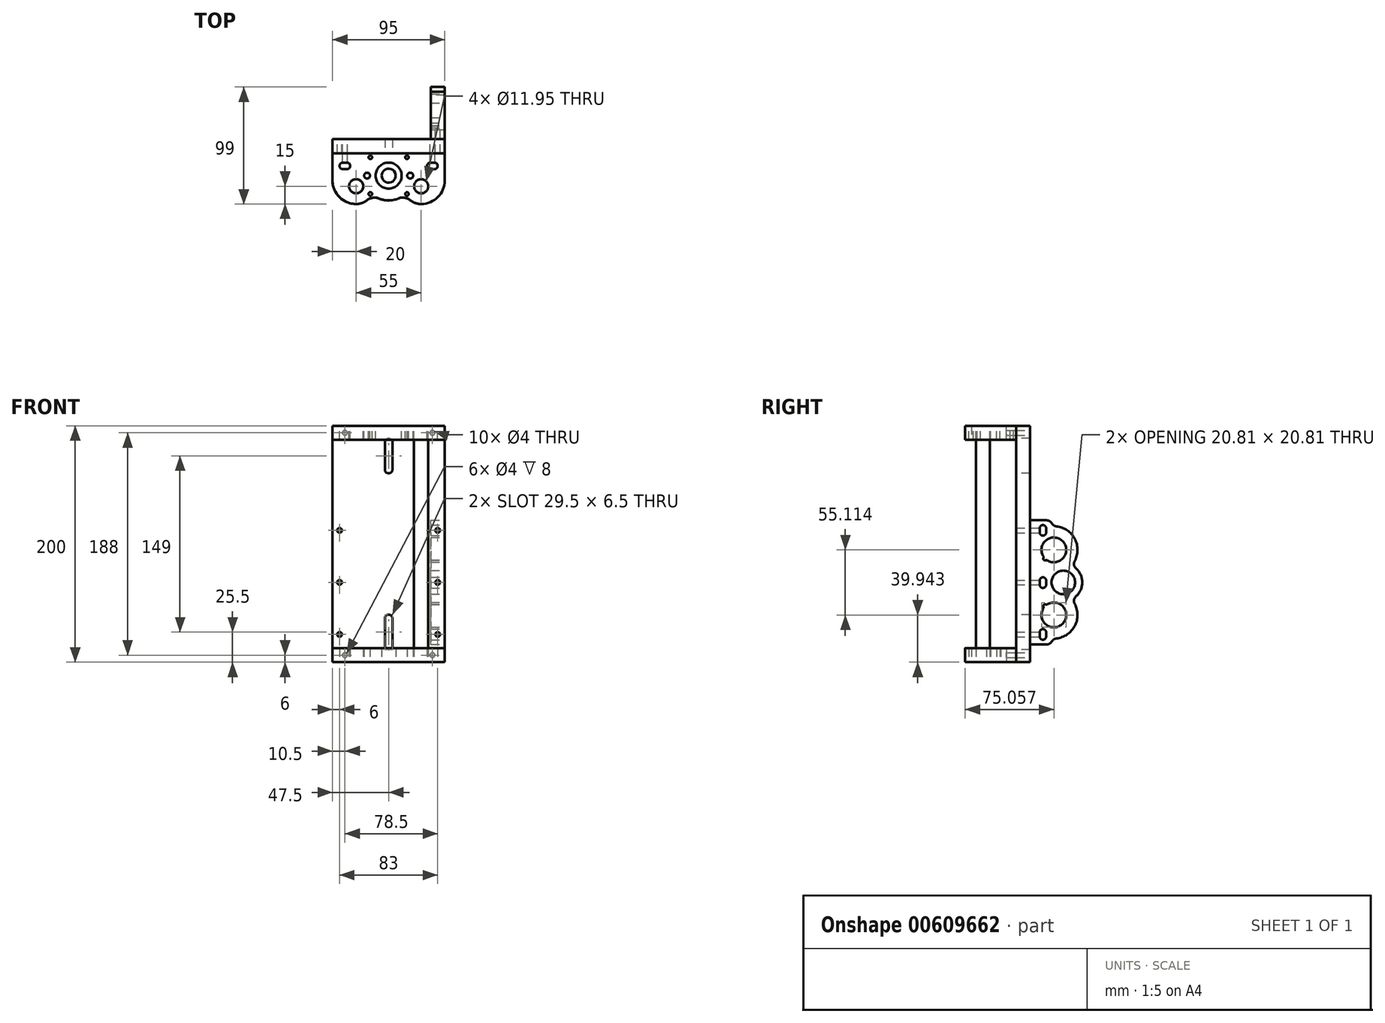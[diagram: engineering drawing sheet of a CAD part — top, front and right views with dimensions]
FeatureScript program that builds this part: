
annotation { "Feature Type Name" : "Feature", "Feature Type Description" : "" }
export const myFeature = defineFeature(function(context is Context, id is Id, definition is map)
    precondition{}
    {
        {
            var Q0;
            Q0=qCreatedBy(makeId("Front.planeOp"),FACE);
            var sketch = newSketch(context, id + "F0", { "sketchPlane" : qUnion([Q0])});
            skLineSegment(sketch, "E0.bottom", {"start": v(47.5, 0) * mm, "end": v(-47.5, 0) * mm});
            skLineSegment(sketch, "E0.top", {"start": v(-47.5, 200) * mm, "end": v(47.5, 200) * mm});
            skLineSegment(sketch, "E0.left", {"start": v(-47.5, 0) * mm, "end": v(-47.5, 200) * mm});
            skLineSegment(sketch, "E0.right", {"start": v(47.5, 0) * mm, "end": v(47.5, 200) * mm});
            skLineSegment(sketch, "E1.left", {"start": v(3.25, 186) * mm, "end": v(3.25, 163) * mm});
            skLineSegment(sketch, "E1.right", {"start": v(-3.25, 186) * mm, "end": v(-3.25, 163) * mm});
            skArc(sketch, "E2", {"start": v(3.25, 186) * mm, "mid": v(0, 189.25) * mm, "end": v(-3.25, 186) * mm});
            skArc(sketch, "E3", {"start": v(-3.25, 163) * mm, "mid": v(0, 159.75) * mm, "end": v(3.25, 163) * mm});
            skLineSegment(sketch, "E4", {"start": v(0, 200) * mm, "end": v(0, 186) * mm, "construction": true});
            skLineSegment(sketch, "E5.left", {"start": v(-3.25, 14) * mm, "end": v(-3.25, 37) * mm});
            skLineSegment(sketch, "E5.right", {"start": v(3.25, 14) * mm, "end": v(3.25, 37) * mm});
            skArc(sketch, "E6", {"start": v(-3.25, 14) * mm, "mid": v(0, 10.75) * mm, "end": v(3.25, 14) * mm});
            skArc(sketch, "E7", {"start": v(3.25, 37) * mm, "mid": v(0, 40.25) * mm, "end": v(-3.25, 37) * mm});
            skLineSegment(sketch, "E8", {"start": v(0, 0) * mm, "end": v(0, 14) * mm, "construction": true});
            skSolve(sketch);
        }
        {
            var Q0;
            Q0=qSketchRegion(id+"F0",true);
            extrude(context, id + "F1", {"entities" : qUnion([Q0]), "oppositeDirection" : true, "depth" : 12 * mm, "offsetDistance" : 25 * mm});
        }
        {
            var Q0;
            Q0=makeQuery(id+"F1.opExtrude","SWEPT_FACE",FACE,{"disambiguationData":[OSD([sQuery(id+"F0.wireOp",EDGE,"E0.top")])]});
            var sketch = newSketch(context, id + "F2", { "sketchPlane" : qUnion([Q0])});
            skLineSegment(sketch, "E9.bottom", {"start": v(-47.5, 0) * mm, "end": v(47.5, 0) * mm});
            skLineSegment(sketch, "E9.top", {"start": v(-27.5, -43) * mm, "end": v(27.5, -43) * mm, "construction": true});
            skLineSegment(sketch, "E9.left", {"start": v(-47.5, 0) * mm, "end": v(-47.5, -23) * mm});
            skLineSegment(sketch, "E9.right", {"start": v(47.5, 0) * mm, "end": v(47.5, -23) * mm});
            skLineSegment(sketch, "E10", {"start": v(0, 0) * mm, "end": v(0, -43) * mm, "construction": true});
            skCircle(sketch, "E11", {"center": v(-27.5, -28) * mm, "radius": 5.97 * mm});
            skCircle(sketch, "E12.MirrorC", {"center": v(27.5, -28) * mm, "radius": 5.97 * mm});
            skArc(sketch, "E13.filletArc", {"start": v(-47.5, -23) * mm, "mid": v(-41.64, -37.14) * mm, "end": v(-27.5, -43) * mm});
            skPoint(sketch, "E14.visualSharp", {"position": v(47.5, -43) * mm});
            skArc(sketch, "E14.filletArc", {"start": v(27.5, -43) * mm, "mid": v(41.64, -37.14) * mm, "end": v(47.5, -23) * mm});
            skCircle(sketch, "E15", {"center": v(0, -19) * mm, "radius": 11 * mm});
            skCircle(sketch, "E16", {"center": v(-18.25, -19) * mm, "radius": 2.5 * mm});
            skCircle(sketch, "E17.MirrorC", {"center": v(18.25, -19) * mm, "radius": 2.5 * mm});
            skLineSegment(sketch, "E18.bottom", {"start": v(-38.75, -8) * mm, "end": v(-35.25, -8) * mm});
            skLineSegment(sketch, "E18.top", {"start": v(-38.75, -13.5) * mm, "end": v(-35.25, -13.5) * mm});
            skArc(sketch, "E19", {"start": v(-38.75, -8) * mm, "mid": v(-41.5, -10.75) * mm, "end": v(-38.75, -13.5) * mm});
            skArc(sketch, "E20", {"start": v(-35.25, -13.5) * mm, "mid": v(-32.5, -10.75) * mm, "end": v(-35.25, -8) * mm});
            skLineSegment(sketch, "E21", {"start": v(-37, -8) * mm, "end": v(-37, -13.5) * mm, "construction": true});
            skArc(sketch, "E22.MirrorCS", {"start": v(35.25, -13.5) * mm, "mid": v(32.5, -10.75) * mm, "end": v(35.25, -8) * mm});
            skLineSegment(sketch, "E23.MirrorCS", {"start": v(38.75, -13.5) * mm, "end": v(35.25, -13.5) * mm});
            skLineSegment(sketch, "E24.MirrorCS", {"start": v(38.75, -8) * mm, "end": v(35.25, -8) * mm});
            skArc(sketch, "E25.MirrorCS", {"start": v(38.75, -8) * mm, "mid": v(41.5, -10.75) * mm, "end": v(38.75, -13.5) * mm});
            skArc(sketch, "E26", {"start": v(-8.94, 0) * mm, "mid": v(0, -40) * mm, "end": v(8.94, 0) * mm});
            skCircle(sketch, "E27", {"center": v(-27.5, -28) * mm, "radius": 15 * mm});
            skCircle(sketch, "E28", {"center": v(27.5, -28) * mm, "radius": 15 * mm});
            skSolve(sketch);
        }
        {
            var Q0;
            Q0=qSketchRegion(id+"F2",true);
            extrude(context, id + "F3", {"entities" : qUnion([Q0]), "oppositeDirection" : true, "depth" : 12 * mm, "offsetDistance" : 25 * mm});
        }
        {
            var Q0;
            Q0=makeQuery(id+"F3.opExtrude","SWEPT_EDGE",EDGE,{"disambiguationData":[OSD([sQuery(id+"F2.wireOp",EDGE,"E26"),sQuery(id+"F2.wireOp",EDGE,"E27")])]});
            var Q1;
            Q1=makeQuery(id+"F3.opExtrude","SWEPT_EDGE",EDGE,{"disambiguationData":[OSD([sQuery(id+"F2.wireOp",EDGE,"E26"),sQuery(id+"F2.wireOp",EDGE,"E28")])]});
            fillet(context, id + "F4", {"entities" : qUnion([Q0, Q1]), "radius" : 10 * mm, "tangentPropagation" : true, "allowEdgeOverflow" : false});
        }
        {
            var Q0;
            Q0=makeQuery(id+"F3.opExtrude","CAP_FACE",FACE,{"disambiguationData":[OSD([sQuery(id+"F2.wireOp",EDGE,"E9.bottom"),sQuery(id+"F2.wireOp",EDGE,"E9.top"),sQuery(id+"F2.wireOp",EDGE,"E9.left"),sQuery(id+"F2.wireOp",EDGE,"E9.right"),sQuery(id+"F2.wireOp",EDGE,"E11"),sQuery(id+"F2.wireOp",EDGE,"E12.MirrorC"),sQuery(id+"F2.wireOp",EDGE,"E13.filletArc"),sQuery(id+"F2.wireOp",EDGE,"E14.filletArc")])],"isStart":true});
            var sketch = newSketch(context, id + "F5", { "sketchPlane" : qUnion([Q0])});
            skCircle(sketch, "E29", {"center": v(27.5, -28) * mm, "radius": 6 * mm});
            skSolve(sketch);
        }
        {
            var Q0;
            Q0=qSketchRegion(id+"F5",true);
            extrude(context, id + "F6", {"entities" : qUnion([Q0]), "oppositeDirection" : true, "depth" : 188 * mm, "offsetDistance" : 25 * mm});
        }
        {
            var Q0;
            Q0=makeQuery(id+"F1.opExtrude","SWEPT_FACE",FACE,{"disambiguationData":[OSD([sQuery(id+"F0.wireOp",EDGE,"E0.right")])]});
            var sketch = newSketch(context, id + "F7", { "sketchPlane" : qUnion([Q0])});
            skLineSegment(sketch, "E30.top", {"start": v(52, 40) * mm, "end": v(52, 67.5) * mm, "construction": true});
            skLineSegment(sketch, "E31", {"start": v(12, 67.5) * mm, "end": v(52, 67.5) * mm, "construction": true});
            skPoint(sketch, "E32.centerSnap0", {"position": v(32, 67.5) * mm});
            skArc(sketch, "E33.filletArc", {"start": v(32, 20) * mm, "mid": v(46.14, 25.86) * mm, "end": v(52, 40) * mm});
            skArc(sketch, "E34.filletArc", {"start": v(52, 95) * mm, "mid": v(46.14, 109.14) * mm, "end": v(32, 115) * mm});
            skArc(sketch, "E35", {"start": v(23.22, 45.7) * mm, "mid": v(39.4, 32.6) * mm, "end": v(26.3, 48.78) * mm});
            skArc(sketch, "E36.MirrorC", {"start": v(23.22, 89.3) * mm, "mid": v(39.4, 102.4) * mm, "end": v(26.3, 86.22) * mm});
            skArc(sketch, "E37", {"start": v(47.07, 53.15) * mm, "mid": v(56, 67.5) * mm, "end": v(47.07, 81.85) * mm});
            skCircle(sketch, "E38", {"center": v(40, 67.5) * mm, "radius": 9.97 * mm});
            skLineSegment(sketch, "E39.bottom", {"start": v(32, 20) * mm, "end": v(28.5, 15) * mm});
            skLineSegment(sketch, "E39.right", {"start": v(28.5, 15) * mm, "end": v(12, 15) * mm});
            skLineSegment(sketch, "E40.bottom", {"start": v(25.5, 25.25) * mm, "end": v(25.5, 21.75) * mm});
            skLineSegment(sketch, "E40.top", {"start": v(20, 25.25) * mm, "end": v(20, 21.75) * mm});
            skArc(sketch, "E41", {"start": v(25.5, 25.25) * mm, "mid": v(22.75, 28) * mm, "end": v(20, 25.25) * mm});
            skArc(sketch, "E42", {"start": v(20, 21.75) * mm, "mid": v(22.75, 19) * mm, "end": v(25.5, 21.75) * mm});
            skLineSegment(sketch, "E43.MirrorCS", {"start": v(32, 115) * mm, "end": v(28.5, 120) * mm});
            skLineSegment(sketch, "E44.MirrorCS", {"start": v(28.5, 120) * mm, "end": v(12, 120) * mm});
            skLineSegment(sketch, "E45.top", {"start": v(20, 69.07) * mm, "end": v(20, 65.57) * mm});
            skArc(sketch, "E46", {"start": v(25.5, 69.07) * mm, "mid": v(22.75, 71.82) * mm, "end": v(20, 69.07) * mm});
            skArc(sketch, "E47", {"start": v(20, 65.57) * mm, "mid": v(22.75, 62.82) * mm, "end": v(25.5, 65.57) * mm});
            skLineSegment(sketch, "E48", {"start": v(20, 23.5) * mm, "end": v(25.5, 23.5) * mm, "construction": true});
            skLineSegment(sketch, "E49.trimOffspring", {"start": v(52, 67.5) * mm, "end": v(52, 95) * mm, "construction": true});
            skLineSegment(sketch, "E50", {"start": v(12, 120) * mm, "end": v(12, 15) * mm});
            skLineSegment(sketch, "E51", {"start": v(32, 40) * mm, "end": v(32, 20) * mm, "construction": true});
            skLineSegment(sketch, "E52", {"start": v(32, 95) * mm, "end": v(32, 40) * mm, "construction": true});
            skArc(sketch, "E53", {"start": v(52, 40) * mm, "mid": v(50.73, 47.02) * mm, "end": v(47.07, 53.15) * mm});
            skArc(sketch, "E54.MirrorCS", {"start": v(52, 95) * mm, "mid": v(50.73, 87.98) * mm, "end": v(47.07, 81.85) * mm});
            skLineSegment(sketch, "E55", {"start": v(32, 95) * mm, "end": v(24.6, 87.6) * mm, "construction": true});
            skArc(sketch, "E56", {"start": v(23.26, 88.29) * mm, "mid": v(23.53, 86.53) * mm, "end": v(25.29, 86.26) * mm});
            skPoint(sketch, "E57.visualSharp", {"position": v(23.61, 88.73) * mm});
            skArc(sketch, "E57.filletArc", {"start": v(23.26, 88.29) * mm, "mid": v(23.38, 88.8) * mm, "end": v(23.22, 89.3) * mm});
            skPoint(sketch, "E58.visualSharp", {"position": v(25.73, 86.61) * mm});
            skArc(sketch, "E58.filletArc", {"start": v(26.3, 86.22) * mm, "mid": v(25.8, 86.38) * mm, "end": v(25.29, 86.26) * mm});
            skArc(sketch, "E59.MirrorCS", {"start": v(26.3, 48.78) * mm, "mid": v(25.8, 48.62) * mm, "end": v(25.29, 48.74) * mm});
            skArc(sketch, "E60.MirrorCS", {"start": v(23.26, 46.71) * mm, "mid": v(23.53, 48.47) * mm, "end": v(25.29, 48.74) * mm});
            skArc(sketch, "E61.MirrorCS", {"start": v(23.26, 46.71) * mm, "mid": v(23.38, 46.2) * mm, "end": v(23.22, 45.7) * mm});
            skLineSegment(sketch, "E62", {"start": v(25.5, 69.07) * mm, "end": v(25.5, 65.57) * mm});
            skArc(sketch, "E63.MirrorCS", {"start": v(25.5, 109.75) * mm, "mid": v(22.75, 107) * mm, "end": v(20, 109.75) * mm});
            skLineSegment(sketch, "E64.MirrorCS", {"start": v(25.5, 109.75) * mm, "end": v(25.5, 113.25) * mm});
            skLineSegment(sketch, "E65.MirrorCS", {"start": v(20, 109.75) * mm, "end": v(20, 113.25) * mm});
            skArc(sketch, "E66.MirrorCS", {"start": v(20, 113.25) * mm, "mid": v(22.75, 116) * mm, "end": v(25.5, 113.25) * mm});
            skSolve(sketch);
        }
        {
            var Q0;
            Q0=qSketchRegion(id+"F7",true);
            extrude(context, id + "F8", {"entities" : qUnion([Q0]), "oppositeDirection" : true, "depth" : 12 * mm, "offsetDistance" : 25 * mm});
        }
        {
            var Q0;
            Q0=makeQuery(id+"F1.opExtrude","SWEPT_FACE",FACE,{"disambiguationData":[OSD([sQuery(id+"F0.wireOp",EDGE,"E0.bottom")])]});
            var sketch = newSketch(context, id + "F9", { "sketchPlane" : qUnion([Q0])});
            skLineSegment(sketch, "E67.0", {"start": v(-47.5, 0) * mm, "end": v(47.5, 0) * mm});
            skArc(sketch, "E67.1", {"start": v(47.5, 23) * mm, "mid": v(41.64, 37.14) * mm, "end": v(27.5, 43) * mm});
            skLineSegment(sketch, "E67.3", {"start": v(47.5, 0) * mm, "end": v(47.5, 23) * mm});
            skArc(sketch, "E67.4", {"start": v(-27.5, 43) * mm, "mid": v(-41.64, 37.14) * mm, "end": v(-47.5, 23) * mm});
            skLineSegment(sketch, "E67.5", {"start": v(-47.5, 23) * mm, "end": v(-47.5, 0) * mm});
            skCircle(sketch, "E68.0", {"center": v(-27.5, 28) * mm, "radius": 5.97 * mm});
            skCircle(sketch, "E69.0", {"center": v(27.5, 28) * mm, "radius": 5.97 * mm});
            skCircle(sketch, "E70.0", {"center": v(-18.25, 19) * mm, "radius": 2.5 * mm});
            skCircle(sketch, "E71.0", {"center": v(18.25, 19) * mm, "radius": 2.5 * mm});
            skCircle(sketch, "E72.0", {"center": v(0, 19) * mm, "radius": 6 * mm});
            skArc(sketch, "E73.0", {"start": v(18.18, 39.76) * mm, "mid": v(22.57, 42.17) * mm, "end": v(27.5, 43) * mm});
            skArc(sketch, "E73.1", {"start": v(-27.5, 43) * mm, "mid": v(-22.57, 42.17) * mm, "end": v(-18.18, 39.76) * mm});
            skArc(sketch, "E73.2", {"start": v(-18.18, 39.76) * mm, "mid": v(-13.34, 37.69) * mm, "end": v(-8.11, 38.37) * mm});
            skArc(sketch, "E73.3", {"start": v(-8.11, 38.37) * mm, "mid": v(0, 40) * mm, "end": v(8.11, 38.37) * mm});
            skArc(sketch, "E73.4", {"start": v(8.11, 38.37) * mm, "mid": v(13.34, 37.69) * mm, "end": v(18.18, 39.76) * mm});
            skArc(sketch, "E74.0", {"start": v(-38.75, 8) * mm, "mid": v(-41.5, 10.75) * mm, "end": v(-38.75, 13.5) * mm});
            skLineSegment(sketch, "E74.1", {"start": v(-38.75, 8) * mm, "end": v(-35.25, 8) * mm});
            skArc(sketch, "E74.2", {"start": v(-35.25, 13.5) * mm, "mid": v(-32.5, 10.75) * mm, "end": v(-35.25, 8) * mm});
            skLineSegment(sketch, "E74.3", {"start": v(-38.75, 13.5) * mm, "end": v(-35.25, 13.5) * mm});
            skArc(sketch, "E75.0", {"start": v(35.25, 13.5) * mm, "mid": v(32.5, 10.75) * mm, "end": v(35.25, 8) * mm});
            skLineSegment(sketch, "E75.1", {"start": v(38.75, 13.5) * mm, "end": v(35.25, 13.5) * mm});
            skArc(sketch, "E75.2", {"start": v(38.75, 8) * mm, "mid": v(41.5, 10.75) * mm, "end": v(38.75, 13.5) * mm});
            skLineSegment(sketch, "E75.3", {"start": v(38.75, 8) * mm, "end": v(35.25, 8) * mm});
            skSolve(sketch);
        }
        {
            var Q0;
            Q0=qSketchRegion(id+"F9",true);
            extrude(context, id + "F10", {"entities" : qUnion([Q0]), "oppositeDirection" : true, "depth" : 12 * mm, "offsetDistance" : 25 * mm});
        }
        {
            var Q0;
            Q0=makeQuery(id+"F1.opExtrude","CAP_FACE",FACE,{"disambiguationData":[OSD([sQuery(id+"F0.wireOp",EDGE,"E0.bottom"),sQuery(id+"F0.wireOp",EDGE,"E0.top"),sQuery(id+"F0.wireOp",EDGE,"E0.left"),sQuery(id+"F0.wireOp",EDGE,"E0.right")])],"isStart":false});
            var sketch = newSketch(context, id + "F11", { "sketchPlane" : qUnion([Q0])});
            skCircle(sketch, "E76", {"center": v(-37, 194) * mm, "radius": 2 * mm});
            skCircle(sketch, "E77", {"center": v(37, 194) * mm, "radius": 2 * mm});
            skLineSegment(sketch, "E78", {"start": v(-47.5, 100) * mm, "end": v(47.5, 100) * mm, "construction": true});
            skCircle(sketch, "E79.MirrorC", {"center": v(37, 6) * mm, "radius": 2 * mm});
            skCircle(sketch, "E80.MirrorC", {"center": v(-37, 6) * mm, "radius": 2 * mm});
            skCircle(sketch, "E81", {"center": v(-41.5, 23.5) * mm, "radius": 2 * mm});
            skCircle(sketch, "E82", {"center": v(-41.5, 111.5) * mm, "radius": 2 * mm});
            skCircle(sketch, "E83", {"center": v(-41.5, 67.5) * mm, "radius": 2 * mm});
            skLineSegment(sketch, "E84", {"start": v(0, 100) * mm, "end": v(0, 0) * mm, "construction": true});
            skCircle(sketch, "E85.MirrorC", {"center": v(41.5, 23.5) * mm, "radius": 2 * mm});
            skCircle(sketch, "E86.MirrorC", {"center": v(41.5, 111.5) * mm, "radius": 2 * mm});
            skCircle(sketch, "E87.MirrorC", {"center": v(41.5, 67.5) * mm, "radius": 2 * mm});
            skSolve(sketch);
        }
        {
            var Q0;
            Q0 = qSketchRegion(id + "F11", true);
            extrude(context, id + "F12", {"entities" : qUnion([Q0]), "operationType" : NewBodyOperationType.REMOVE, "oppositeDirection" : true, "depth" : 25 * mm, "offsetDistance" : 25 * mm, "hasSecondDirection" : true, "secondDirectionOppositeDirection" : false, "secondDirectionDepth" : 10 * mm});
        }
        {
            var Q0;
            Q0=makeQuery(id+"F3.opExtrude","CAP_FACE",FACE,{"disambiguationData":[OSD([sQuery(id+"F2.wireOp",EDGE,"E9.bottom"),sQuery(id+"F2.wireOp",EDGE,"E9.left"),sQuery(id+"F2.wireOp",EDGE,"E9.right"),sQuery(id+"F2.wireOp",EDGE,"E11"),sQuery(id+"F2.wireOp",EDGE,"E12.MirrorC"),sQuery(id+"F2.wireOp",EDGE,"E13.filletArc"),sQuery(id+"F2.wireOp",EDGE,"E14.filletArc"),sQuery(id+"F2.wireOp",EDGE,"E15"),sQuery(id+"F2.wireOp",EDGE,"E16"),sQuery(id+"F2.wireOp",EDGE,"E17.MirrorC"),sQuery(id+"F2.wireOp",EDGE,"E18.bottom"),sQuery(id+"F2.wireOp",EDGE,"E18.top"),sQuery(id+"F2.wireOp",EDGE,"E19"),sQuery(id+"F2.wireOp",EDGE,"E20"),sQuery(id+"F2.wireOp",EDGE,"E22.MirrorCS"),sQuery(id+"F2.wireOp",EDGE,"E23.MirrorCS"),sQuery(id+"F2.wireOp",EDGE,"E24.MirrorCS"),sQuery(id+"F2.wireOp",EDGE,"E25.MirrorCS"),sQuery(id+"F2.wireOp",EDGE,"E26"),sQuery(id+"F2.wireOp",EDGE,"E27"),sQuery(id+"F2.wireOp",EDGE,"E28")])],"isStart":true});
            var sketch = newSketch(context, id + "F13", { "sketchPlane" : qUnion([Q0])});
            skLineSegment(sketch, "E88.bottom", {"start": v(-15.5, -3.5) * mm, "end": v(15.5, -3.5) * mm, "construction": true});
            skLineSegment(sketch, "E88.top", {"start": v(-15.5, -34.5) * mm, "end": v(15.5, -34.5) * mm, "construction": true});
            skLineSegment(sketch, "E88.left", {"start": v(-15.5, -3.5) * mm, "end": v(-15.5, -34.5) * mm, "construction": true});
            skLineSegment(sketch, "E88.right", {"start": v(15.5, -3.5) * mm, "end": v(15.5, -34.5) * mm, "construction": true});
            skLineSegment(sketch, "E89", {"start": v(-15.5, -19) * mm, "end": v(15.5, -19) * mm, "construction": true});
            skPoint(sketch, "E90", {"position": v(0, -19) * mm});
            skCircle(sketch, "E91", {"center": v(-15.5, -3.5) * mm, "radius": 1.5 * mm});
            skCircle(sketch, "E92.1.0", {"center": v(-15.5, -34.5) * mm, "radius": 1.5 * mm});
            skCircle(sketch, "E92.2.0", {"center": v(15.5, -34.5) * mm, "radius": 1.5 * mm});
            skCircle(sketch, "E92.3.0", {"center": v(15.5, -3.5) * mm, "radius": 1.5 * mm});
            skSolve(sketch);
        }
        {
            var Q0;
            Q0 = qSketchRegion(id + "F13", true);
            extrude(context, id + "F14", {"entities" : qUnion([Q0]), "operationType" : NewBodyOperationType.REMOVE, "oppositeDirection" : true, "depth" : 25 * mm, "offsetDistance" : 25 * mm});
        }
        {
            var Q0;
            Q0=makeQuery(id+"F8.opExtrude","SWEPT_EDGE",EDGE,{"disambiguationData":[OSD([sQuery(id+"F7.wireOp",EDGE,"E33.filletArc"),sQuery(id+"F7.wireOp",EDGE,"E39.bottom")])]});
            var Q1;
            Q1=makeQuery(id+"F8.opExtrude","SWEPT_EDGE",EDGE,{"disambiguationData":[OSD([sQuery(id+"F7.wireOp",EDGE,"E39.bottom"),sQuery(id+"F7.wireOp",EDGE,"E39.right")])]});
            var Q2;
            Q2=makeQuery(id+"F8.opExtrude","SWEPT_EDGE",EDGE,{"disambiguationData":[OSD([sQuery(id+"F7.wireOp",EDGE,"E34.filletArc"),sQuery(id+"F7.wireOp",EDGE,"E43.MirrorCS")])]});
            var Q3;
            Q3=makeQuery(id+"F8.opExtrude","SWEPT_EDGE",EDGE,{"disambiguationData":[OSD([sQuery(id+"F7.wireOp",EDGE,"E43.MirrorCS"),sQuery(id+"F7.wireOp",EDGE,"E44.MirrorCS")])]});
            fillet(context, id + "F15", {"entities" : qUnion([Q0, Q1, Q2, Q3]), "radius" : 5 * mm, "tangentPropagation" : true, "allowEdgeOverflow" : false});
        }
        {
            var Q0;
            Q0=makeQuery(id+"F8.opExtrude","SWEPT_EDGE",EDGE,{"disambiguationData":[OSD([sQuery(id+"F7.wireOp",EDGE,"E37"),sQuery(id+"F7.wireOp",EDGE,"E54.MirrorCS")])]});
            var Q1;
            Q1=makeQuery(id+"F8.opExtrude","SWEPT_EDGE",EDGE,{"disambiguationData":[OSD([sQuery(id+"F7.wireOp",EDGE,"E37"),sQuery(id+"F7.wireOp",EDGE,"E53")])]});
            var Q2;
            Q2=makeQuery(id+"F8.opExtrude","SWEPT_EDGE",EDGE,{"disambiguationData":[OSD([sQuery(id+"F7.wireOp",EDGE,"E38"),sQuery(id+"F7.wireOp",EDGE,"E45.bottom"),sQuery(id+"F7.wireOp",EDGE,"E46")])]});
            var Q3;
            Q3=makeQuery(id+"F8.opExtrude","SWEPT_EDGE",EDGE,{"disambiguationData":[OSD([sQuery(id+"F7.wireOp",EDGE,"E38"),sQuery(id+"F7.wireOp",EDGE,"E45.bottom"),sQuery(id+"F7.wireOp",EDGE,"E47")])]});
            fillet(context, id + "F16", {"entities" : qUnion([Q0, Q1, Q2, Q3]), "radius" : 5 * mm, "tangentPropagation" : true, "allowEdgeOverflow" : false});
        }
    });
